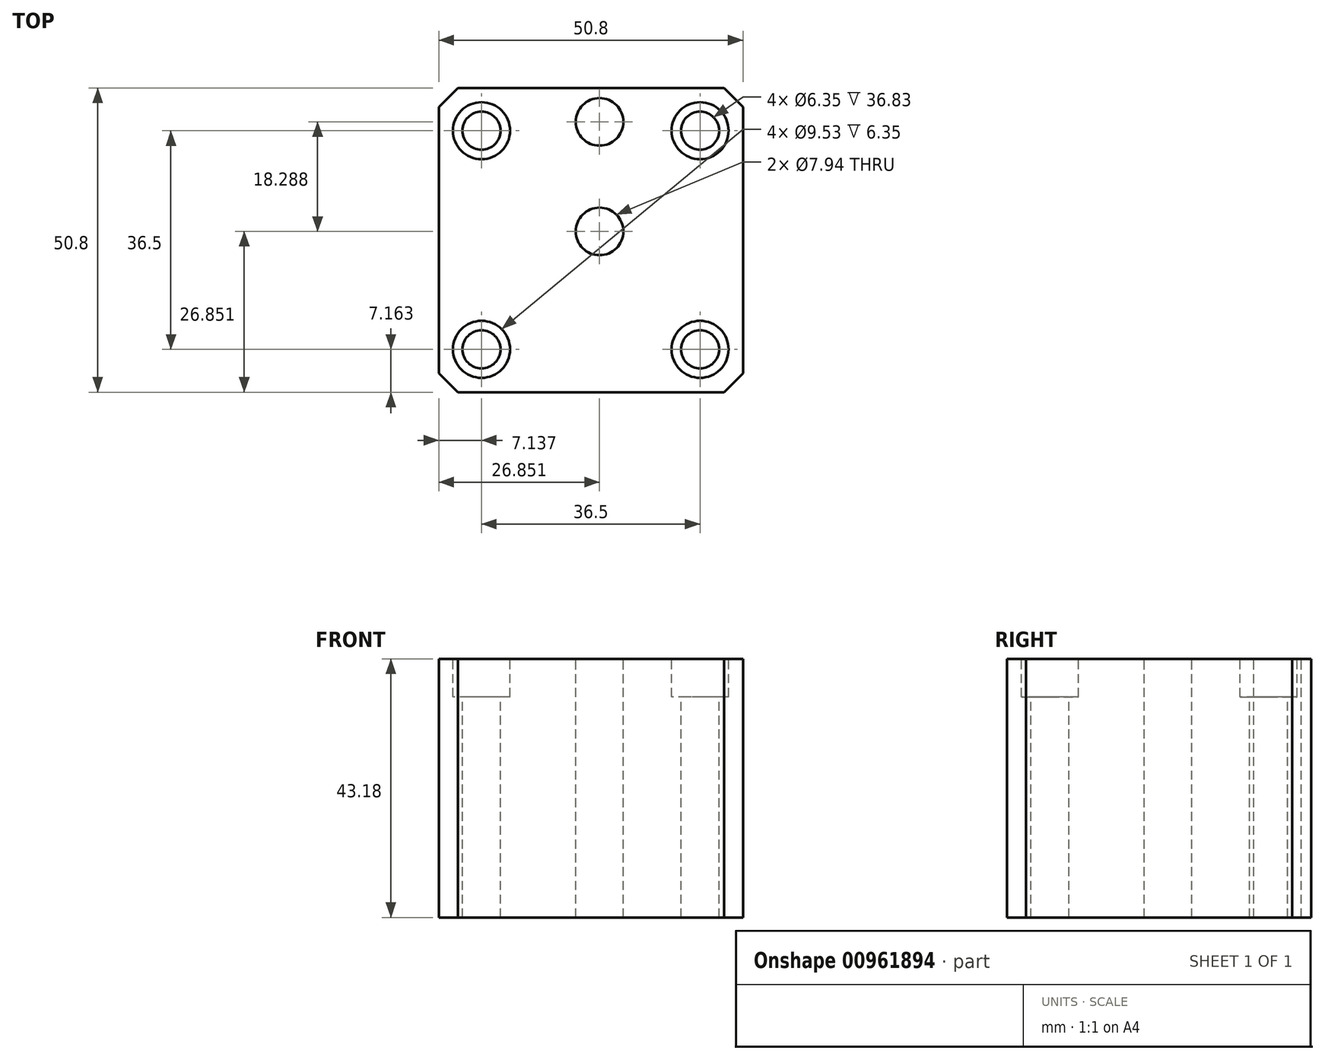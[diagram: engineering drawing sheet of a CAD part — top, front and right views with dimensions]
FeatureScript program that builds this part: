
annotation { "Feature Type Name" : "Feature", "Feature Type Description" : "" }
export const myFeature = defineFeature(function(context is Context, id is Id, definition is map)
    precondition{}
    {
        {
            var Q0;
            Q0=qCreatedBy(makeId("Front.planeOp"),FACE);
            var sketch = newSketch(context, id + "F0", { "sketchPlane" : qUnion([Q0])});
            skLineSegment(sketch, "E0", {"start": v(0, 0) * mm, "end": v(50.8, 0) * mm});
            skLineSegment(sketch, "E1", {"start": v(50.8, 0) * mm, "end": v(50.8, -43.18) * mm});
            skLineSegment(sketch, "E2", {"start": v(50.8, -43.18) * mm, "end": v(0, -43.18) * mm});
            skLineSegment(sketch, "E3", {"start": v(0, -43.18) * mm, "end": v(0, 0) * mm});
            skSolve(sketch);
        }
        {
            var Q0;
            Q0=makeQuery(id+"F0.imprint","IMPRINT",FACE,{"disambiguationData":[TD([[makeQuery(id+"F0.imprint","IMPRINT",EDGE,{"derivedFrom":sQuery(id+"F0.wireOp",EDGE,"E0")}),-1.0]])]});
            extrude(context, id + "F1", {"entities" : qUnion([Q0]), "oppositeDirection" : true, "depth" : 50.8 * mm, "offsetDistance" : 25.4 * mm});
        }
        {
            var Q0;
            Q0=makeQuery(id+"F1.opExtrude","SWEPT_FACE",FACE,{"disambiguationData":[OSD([sQuery(id+"F0.wireOp",EDGE,"E0")])]});
            var sketch = newSketch(context, id + "F2", { "sketchPlane" : qUnion([Q0])});
            skPoint(sketch, "E4", {"position": v(7.14, 43.66) * mm});
            skPoint(sketch, "E5", {"position": v(43.64, 43.66) * mm});
            skPoint(sketch, "E6", {"position": v(7.14, 7.16) * mm});
            skPoint(sketch, "E7", {"position": v(43.64, 7.16) * mm});
            skSolve(sketch);
        }
        {
            var Q0;
            Q0=sQuery(id+"F2.wireOp",VERTEX,"E6");
            var Q1;
            Q1=sQuery(id+"F2.wireOp",VERTEX,"E4");
            var Q2;
            Q2=sQuery(id+"F2.wireOp",VERTEX,"E5");
            var Q3;
            Q3=sQuery(id+"F2.wireOp",VERTEX,"E7");
            var Q4;
            Q4=makeQuery(id+"F1.opExtrude","SWEPT_BODY",BODY,{"disambiguationData":[OSD([sQuery(id+"F0.wireOp",EDGE,"E0"),sQuery(id+"F0.wireOp",EDGE,"E1"),sQuery(id+"F0.wireOp",EDGE,"E2"),sQuery(id+"F0.wireOp",EDGE,"E3")])]});
            hole(context, id + "F3", {"style" : HoleStyle.C_BORE, "endStyle" : HoleEndStyle.THROUGH, "holeDiameter" : 6.35 * mm, "cBoreDiameter" : 9.52 * mm, "cBoreDepth" : 6.35 * mm, "majorDiameter" : 9.52 * mm, "isTappedThrough" : true, "tappedDepth" : 12.7 * mm, "tapClearance" : 3, "locations" : qUnion([Q0, Q1, Q2, Q3]), "scope" : qUnion([Q4])});
        }
        {
            var Q0;
            {var subQ0=sQuery(id+"F0.wireOp",EDGE,"E0");Q0=makeQuery(id+"F2.imprint","IMPRINT",FACE,{"disambiguationData":[TD([[makeQuery(id+"F2.imprint","IMPRINT",EDGE,{"derivedFrom":makeQuery(id+"F1.opExtrude","CAP_EDGE",EDGE,{"disambiguationData":[OSD([subQ0])],"isStart":true})}),1.0]])]});}
            var sketch = newSketch(context, id + "F4", { "sketchPlane" : qUnion([Q0])});
            skLineSegment(sketch, "E8", {"start": v(0, 53.7) * mm, "end": v(53.7, 0) * mm});
            skPoint(sketch, "E9", {"position": v(26.85, 26.85) * mm});
            skPoint(sketch, "E10", {"position": v(26.85, 45.14) * mm});
            skSolve(sketch);
        }
        {
            var Q0;
            Q0=sQuery(id+"F4.wireOp",VERTEX,"E9");
            var Q1;
            Q1=sQuery(id+"F4.wireOp",VERTEX,"E10");
            var Q2;
            Q2=makeQuery(id+"F1.opExtrude","SWEPT_BODY",BODY,{"disambiguationData":[OSD([sQuery(id+"F0.wireOp",EDGE,"E0"),sQuery(id+"F0.wireOp",EDGE,"E1"),sQuery(id+"F0.wireOp",EDGE,"E2"),sQuery(id+"F0.wireOp",EDGE,"E3")])]});
            hole(context, id + "F5", {"style" : HoleStyle.SIMPLE, "endStyle" : HoleEndStyle.THROUGH, "holeDiameter" : 7.94 * mm, "majorDiameter" : 6.35 * mm, "isTappedThrough" : true, "tappedDepth" : 12.7 * mm, "tapClearance" : 3, "locations" : qUnion([Q0, Q1]), "scope" : qUnion([Q2])});
        }
        {
            var Q0;
            Q0=makeQuery(id+"F1.opExtrude","CAP_EDGE",EDGE,{"disambiguationData":[OSD([sQuery(id+"F0.wireOp",EDGE,"E1")])],"isStart":false});
            var Q1;
            Q1=makeQuery(id+"F1.opExtrude","CAP_EDGE",EDGE,{"disambiguationData":[OSD([sQuery(id+"F0.wireOp",EDGE,"E1")])],"isStart":true});
            var Q2;
            Q2=makeQuery(id+"F1.opExtrude","CAP_EDGE",EDGE,{"disambiguationData":[OSD([sQuery(id+"F0.wireOp",EDGE,"E3")])],"isStart":false});
            var Q3;
            Q3=makeQuery(id+"F1.opExtrude","CAP_EDGE",EDGE,{"disambiguationData":[OSD([sQuery(id+"F0.wireOp",EDGE,"E3")])],"isStart":true});
            chamfer(context, id + "F6", {"entities" : qUnion([Q0, Q1, Q2, Q3]), "width" : 3.17 * mm, "tangentPropagation" : true});
        }
    });
